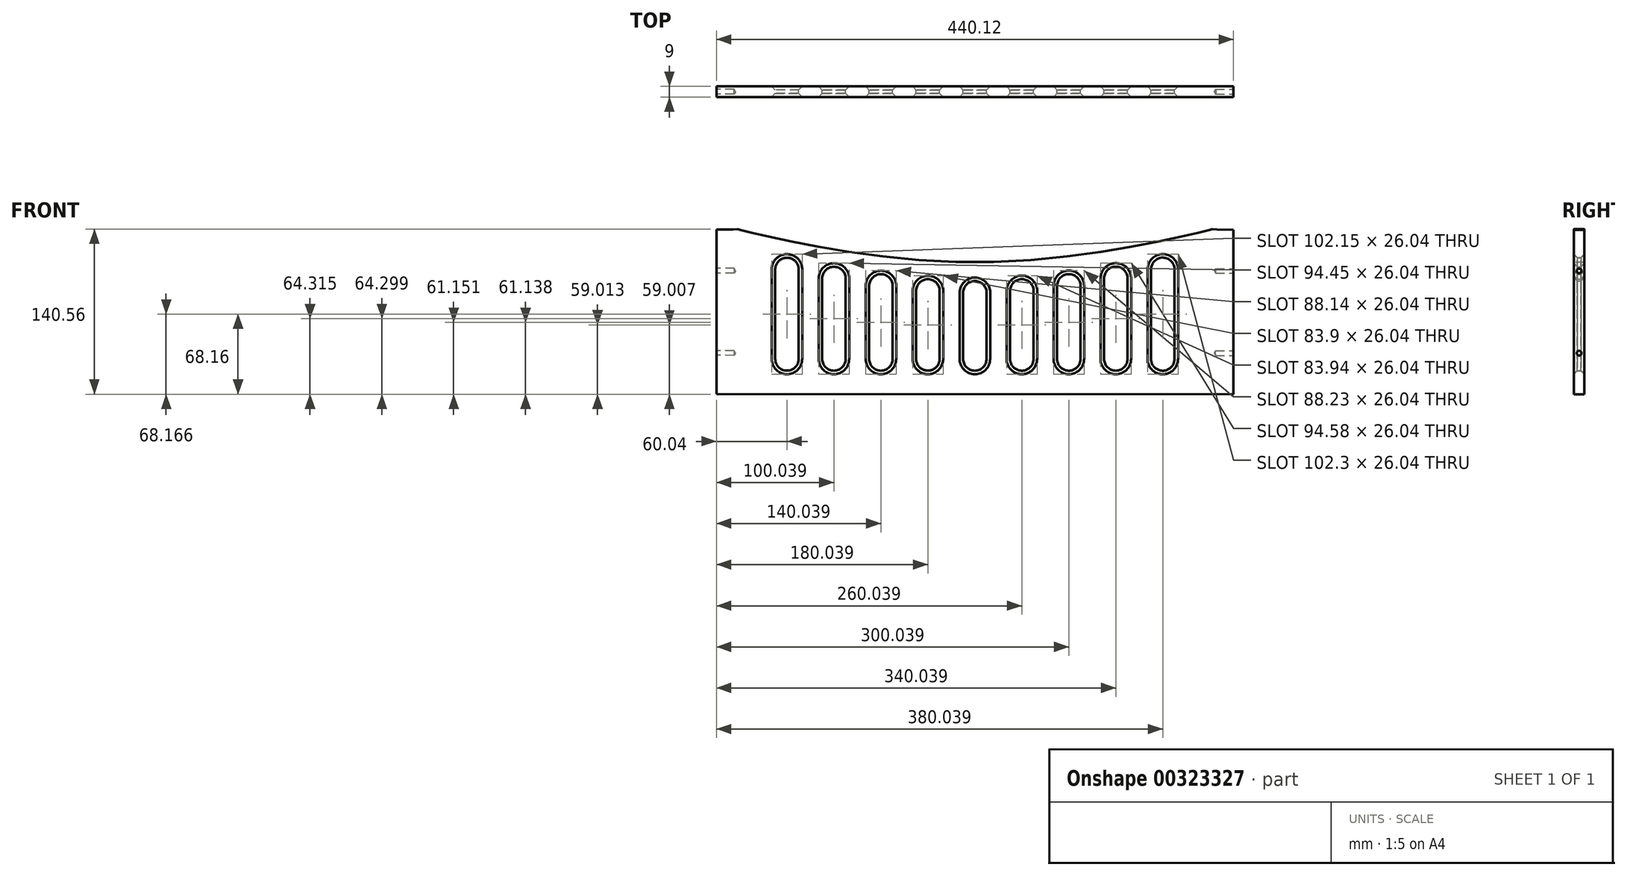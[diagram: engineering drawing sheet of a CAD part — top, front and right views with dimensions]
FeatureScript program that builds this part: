
annotation { "Feature Type Name" : "Feature", "Feature Type Description" : "" }
export const myFeature = defineFeature(function(context is Context, id is Id, definition is map)
    precondition{}
    {
        {
            var Q0;
            Q0=qCreatedBy(makeId("Front.planeOp"),FACE);
            var sketch = newSketch(context, id + "F0", { "sketchPlane" : qUnion([Q0])});
            skLineSegment(sketch, "E0.bottom", {"start": v(219.94, -70.05) * mm, "end": v(-220.06, -69.95) * mm});
            skLineSegment(sketch, "E0.left", {"start": v(219.94, -70.05) * mm, "end": v(220.06, 69.95) * mm});
            skLineSegment(sketch, "E0.right", {"start": v(-220.06, -69.95) * mm, "end": v(-219.94, 70.05) * mm});
            skPoint(sketch, "E0.middle", {"position": v(0, 0) * mm});
            skFitSpline(sketch, "E1", {"points": [v(-219.94, 70.05) * mm, v(-199.94, 70.05) * mm, v(0, 42.34) * mm, v(200.06, 70.05) * mm, v(220.06, 69.95) * mm], "startDerivative": vector(501.28, 0) * mm, "endDerivative": vector(501.28, -2.26) * mm});
            skLineSegment(sketch, "E2", {"start": v(0, 16.34) * mm, "end": v(-0.04, -40) * mm});
            skLineSegment(sketch, "E3.4.0.1", {"start": v(-170, 16.34) * mm, "end": v(-170, 16.34) * mm});
            skLineSegment(sketch, "E4", {"start": v(-120, 28.47) * mm, "end": v(-120.04, -39.98) * mm});
            skLineSegment(sketch, "E5", {"start": v(-80, 22.16) * mm, "end": v(-80.04, -39.98) * mm});
            skLineSegment(sketch, "E6", {"start": v(-40, 17.9) * mm, "end": v(-40.04, -40) * mm});
            skLineSegment(sketch, "E7", {"start": v(40, 17.93) * mm, "end": v(39.96, -40) * mm});
            skLineSegment(sketch, "E8", {"start": v(80, 22.22) * mm, "end": v(79.96, -40.02) * mm});
            skLineSegment(sketch, "E9", {"start": v(120, 28.55) * mm, "end": v(119.96, -40.02) * mm});
            skLineSegment(sketch, "E10", {"start": v(160, 36.27) * mm, "end": v(159.96, -40.03) * mm});
            skArc(sketch, "E11.0.startCap", {"start": v(-170, 36.19) * mm, "mid": v(-160, 46.18) * mm, "end": v(-150, 36.18) * mm});
            skArc(sketch, "E11.0.endCap", {"start": v(-150.05, -39.97) * mm, "mid": v(-160.05, -49.96) * mm, "end": v(-170.04, -39.96) * mm});
            skLineSegment(sketch, "E11.0.left", {"start": v(-150, 36.18) * mm, "end": v(-150.05, -39.97) * mm});
            skLineSegment(sketch, "E11.0.right", {"start": v(-170, 36.19) * mm, "end": v(-170.04, -39.96) * mm});
            skArc(sketch, "E11.1.startCap", {"start": v(-130, 28.48) * mm, "mid": v(-120, 38.47) * mm, "end": v(-110, 28.47) * mm});
            skArc(sketch, "E11.1.endCap", {"start": v(-110.04, -39.98) * mm, "mid": v(-120.05, -49.98) * mm, "end": v(-130.04, -39.97) * mm});
            skLineSegment(sketch, "E11.1.left", {"start": v(-110, 28.47) * mm, "end": v(-110.04, -39.98) * mm});
            skLineSegment(sketch, "E11.1.right", {"start": v(-130, 28.48) * mm, "end": v(-130.04, -39.97) * mm});
            skArc(sketch, "E11.2.startCap", {"start": v(-90, 22.17) * mm, "mid": v(-80, 32.16) * mm, "end": v(-70, 22.15) * mm});
            skArc(sketch, "E11.2.endCap", {"start": v(-70.04, -40) * mm, "mid": v(-80.05, -49.98) * mm, "end": v(-90.04, -39.98) * mm});
            skLineSegment(sketch, "E11.2.left", {"start": v(-70, 22.15) * mm, "end": v(-70.04, -40) * mm});
            skLineSegment(sketch, "E11.2.right", {"start": v(-90, 22.17) * mm, "end": v(-90.04, -39.98) * mm});
            skArc(sketch, "E11.3.startCap", {"start": v(-50, 17.91) * mm, "mid": v(-40, 27.9) * mm, "end": v(-30, 17.9) * mm});
            skArc(sketch, "E11.3.endCap", {"start": v(-30.04, -40) * mm, "mid": v(-40.05, -50) * mm, "end": v(-50.04, -39.98) * mm});
            skLineSegment(sketch, "E11.3.left", {"start": v(-30, 17.9) * mm, "end": v(-30.04, -40) * mm});
            skLineSegment(sketch, "E11.3.right", {"start": v(-50, 17.91) * mm, "end": v(-50.04, -39.98) * mm});
            skArc(sketch, "E11.4.startCap", {"start": v(-10, 16.34) * mm, "mid": v(0, 26.34) * mm, "end": v(10, 16.33) * mm});
            skArc(sketch, "E11.4.endCap", {"start": v(9.96, -40) * mm, "mid": v(-0.05, -50) * mm, "end": v(-10.04, -40) * mm});
            skLineSegment(sketch, "E11.4.left", {"start": v(10, 16.33) * mm, "end": v(9.96, -40) * mm});
            skLineSegment(sketch, "E11.4.right", {"start": v(-10, 16.34) * mm, "end": v(-10.04, -40) * mm});
            skArc(sketch, "E11.5.startCap", {"start": v(30, 17.94) * mm, "mid": v(40, 27.93) * mm, "end": v(50, 17.93) * mm});
            skArc(sketch, "E11.5.endCap", {"start": v(49.96, -40.02) * mm, "mid": v(39.95, -50) * mm, "end": v(29.96, -40) * mm});
            skLineSegment(sketch, "E11.5.left", {"start": v(50, 17.93) * mm, "end": v(49.96, -40.02) * mm});
            skLineSegment(sketch, "E11.5.right", {"start": v(30, 17.94) * mm, "end": v(29.96, -40) * mm});
            skArc(sketch, "E11.6.startCap", {"start": v(70, 22.23) * mm, "mid": v(80, 32.22) * mm, "end": v(90, 22.21) * mm});
            skArc(sketch, "E11.6.endCap", {"start": v(89.96, -40.02) * mm, "mid": v(79.95, -50.02) * mm, "end": v(69.96, -40) * mm});
            skLineSegment(sketch, "E11.6.left", {"start": v(90, 22.21) * mm, "end": v(89.96, -40.02) * mm});
            skLineSegment(sketch, "E11.6.right", {"start": v(70, 22.23) * mm, "end": v(69.96, -40) * mm});
            skArc(sketch, "E11.7.startCap", {"start": v(110, 28.56) * mm, "mid": v(120, 38.55) * mm, "end": v(130, 28.55) * mm});
            skArc(sketch, "E11.7.endCap", {"start": v(129.96, -40.03) * mm, "mid": v(119.95, -50.02) * mm, "end": v(109.96, -40.02) * mm});
            skLineSegment(sketch, "E11.7.left", {"start": v(130, 28.55) * mm, "end": v(129.96, -40.03) * mm});
            skLineSegment(sketch, "E11.7.right", {"start": v(110, 28.56) * mm, "end": v(109.96, -40.02) * mm});
            skArc(sketch, "E11.8.startCap", {"start": v(150, 36.27) * mm, "mid": v(160, 46.27) * mm, "end": v(170, 36.26) * mm});
            skArc(sketch, "E11.8.endCap", {"start": v(169.96, -40.04) * mm, "mid": v(159.95, -50.03) * mm, "end": v(149.96, -40.03) * mm});
            skLineSegment(sketch, "E11.8.left", {"start": v(170, 36.26) * mm, "end": v(169.96, -40.04) * mm});
            skLineSegment(sketch, "E11.8.right", {"start": v(150, 36.27) * mm, "end": v(149.96, -40.03) * mm});
            skSolve(sketch);
        }
        {
            var Q0;
            Q0=makeQuery(id+"F0.imprint","IMPRINT",FACE,{"disambiguationData":[TD([[makeQuery(id+"F0.imprint","IMPRINT",EDGE,{"derivedFrom":sQuery(id+"F0.wireOp",EDGE,"E0.bottom")}),-1.0]])]});
            extrude(context, id + "F1", {"entities" : qUnion([Q0]), "depth" : 9 * mm});
        }
        {
            var Q0;
            Q0=makeQuery(id+"F1.opExtrude","CAP_EDGE",EDGE,{"disambiguationData":[OSD([sQuery(id+"F0.wireOp",EDGE,"E11.0.startCap")])],"isStart":false});
            var Q1;
            Q1=makeQuery(id+"F1.opExtrude","CAP_EDGE",EDGE,{"disambiguationData":[OSD([sQuery(id+"F0.wireOp",EDGE,"E11.1.left")])],"isStart":false});
            var Q2;
            Q2=makeQuery(id+"F1.opExtrude","CAP_EDGE",EDGE,{"disambiguationData":[OSD([sQuery(id+"F0.wireOp",EDGE,"E11.2.left")])],"isStart":false});
            var Q3;
            Q3=makeQuery(id+"F1.opExtrude","CAP_EDGE",EDGE,{"disambiguationData":[OSD([sQuery(id+"F0.wireOp",EDGE,"E11.3.left")])],"isStart":false});
            var Q4;
            Q4=makeQuery(id+"F1.opExtrude","CAP_EDGE",EDGE,{"disambiguationData":[OSD([sQuery(id+"F0.wireOp",EDGE,"E11.4.left")])],"isStart":false});
            var Q5;
            Q5=makeQuery(id+"F1.opExtrude","CAP_EDGE",EDGE,{"disambiguationData":[OSD([sQuery(id+"F0.wireOp",EDGE,"E11.5.left")])],"isStart":true});
            var Q6;
            Q6=makeQuery(id+"F1.opExtrude","CAP_EDGE",EDGE,{"disambiguationData":[OSD([sQuery(id+"F0.wireOp",EDGE,"E11.5.left")])],"isStart":false});
            var Q7;
            Q7=makeQuery(id+"F1.opExtrude","CAP_EDGE",EDGE,{"disambiguationData":[OSD([sQuery(id+"F0.wireOp",EDGE,"E11.6.left")])],"isStart":true});
            var Q8;
            Q8=makeQuery(id+"F1.opExtrude","CAP_EDGE",EDGE,{"disambiguationData":[OSD([sQuery(id+"F0.wireOp",EDGE,"E11.6.left")])],"isStart":false});
            var Q9;
            Q9=makeQuery(id+"F1.opExtrude","CAP_EDGE",EDGE,{"disambiguationData":[OSD([sQuery(id+"F0.wireOp",EDGE,"E11.7.left")])],"isStart":false});
            var Q10;
            Q10=makeQuery(id+"F1.opExtrude","CAP_EDGE",EDGE,{"disambiguationData":[OSD([sQuery(id+"F0.wireOp",EDGE,"E11.7.left")])],"isStart":true});
            var Q11;
            Q11=makeQuery(id+"F1.opExtrude","CAP_EDGE",EDGE,{"disambiguationData":[OSD([sQuery(id+"F0.wireOp",EDGE,"E11.8.right")])],"isStart":false});
            var Q12;
            Q12=makeQuery(id+"F1.opExtrude","CAP_EDGE",EDGE,{"disambiguationData":[OSD([sQuery(id+"F0.wireOp",EDGE,"E11.8.left")])],"isStart":true});
            var Q13;
            Q13=makeQuery(id+"F1.opExtrude","CAP_EDGE",EDGE,{"disambiguationData":[OSD([sQuery(id+"F0.wireOp",EDGE,"E11.0.right")])],"isStart":true});
            var Q14;
            Q14=makeQuery(id+"F1.opExtrude","CAP_EDGE",EDGE,{"disambiguationData":[OSD([sQuery(id+"F0.wireOp",EDGE,"E11.1.right")])],"isStart":true});
            var Q15;
            Q15=makeQuery(id+"F1.opExtrude","CAP_EDGE",EDGE,{"disambiguationData":[OSD([sQuery(id+"F0.wireOp",EDGE,"E11.2.right")])],"isStart":true});
            var Q16;
            Q16=makeQuery(id+"F1.opExtrude","CAP_EDGE",EDGE,{"disambiguationData":[OSD([sQuery(id+"F0.wireOp",EDGE,"E11.3.right")])],"isStart":true});
            var Q17;
            Q17=makeQuery(id+"F1.opExtrude","CAP_EDGE",EDGE,{"disambiguationData":[OSD([sQuery(id+"F0.wireOp",EDGE,"E11.4.right")])],"isStart":true});
            chamfer(context, id + "F2", {"entities" : qUnion([Q0, Q1, Q2, Q3, Q4, Q5, Q6, Q7, Q8, Q9, Q10, Q11, Q12, Q13, Q14, Q15, Q16, Q17]), "width" : 3 * mm, "tangentPropagation" : true});
        }
        {
            var Q0;
            Q0=makeQuery(id+"F1.opExtrude","SWEPT_FACE",FACE,{"disambiguationData":[OSD([sQuery(id+"F0.wireOp",EDGE,"E0.right")])]});
            var sketch = newSketch(context, id + "F3", { "sketchPlane" : qUnion([Q0])});
            skLineSegment(sketch, "E12", {"start": v(4.5, 69.85) * mm, "end": v(4.5, -70.15) * mm});
            skPoint(sketch, "E13", {"position": v(4.5, 34.85) * mm});
            skPoint(sketch, "E14", {"position": v(4.5, -35.15) * mm});
            skSolve(sketch);
        }
        {
            var Q0;
            Q0=sQuery(id+"F3.wireOp",VERTEX,"E13");
            var Q1;
            Q1=sQuery(id+"F3.wireOp",VERTEX,"E14");
            var Q2;
            Q2=makeQuery(id+"F1.opExtrude","SWEPT_BODY",BODY,{"disambiguationData":[OSD([sQuery(id+"F0.wireOp",EDGE,"E0.bottom"),sQuery(id+"F0.wireOp",EDGE,"E0.left"),sQuery(id+"F0.wireOp",EDGE,"E0.right"),sQuery(id+"F0.wireOp",EDGE,"E1"),sQuery(id+"F0.wireOp",EDGE,"E11.0.startCap"),sQuery(id+"F0.wireOp",EDGE,"E11.0.endCap"),sQuery(id+"F0.wireOp",EDGE,"E11.0.left"),sQuery(id+"F0.wireOp",EDGE,"E11.0.right"),sQuery(id+"F0.wireOp",EDGE,"E11.1.startCap"),sQuery(id+"F0.wireOp",EDGE,"E11.1.endCap"),sQuery(id+"F0.wireOp",EDGE,"E11.1.left"),sQuery(id+"F0.wireOp",EDGE,"E11.1.right"),sQuery(id+"F0.wireOp",EDGE,"E11.2.startCap"),sQuery(id+"F0.wireOp",EDGE,"E11.2.endCap"),sQuery(id+"F0.wireOp",EDGE,"E11.2.left"),sQuery(id+"F0.wireOp",EDGE,"E11.2.right"),sQuery(id+"F0.wireOp",EDGE,"E11.3.startCap"),sQuery(id+"F0.wireOp",EDGE,"E11.3.endCap"),sQuery(id+"F0.wireOp",EDGE,"E11.3.left"),sQuery(id+"F0.wireOp",EDGE,"E11.3.right"),sQuery(id+"F0.wireOp",EDGE,"E11.4.startCap"),sQuery(id+"F0.wireOp",EDGE,"E11.4.endCap"),sQuery(id+"F0.wireOp",EDGE,"E11.4.left"),sQuery(id+"F0.wireOp",EDGE,"E11.4.right"),sQuery(id+"F0.wireOp",EDGE,"E11.5.startCap"),sQuery(id+"F0.wireOp",EDGE,"E11.5.endCap"),sQuery(id+"F0.wireOp",EDGE,"E11.5.left"),sQuery(id+"F0.wireOp",EDGE,"E11.5.right"),sQuery(id+"F0.wireOp",EDGE,"E11.6.startCap"),sQuery(id+"F0.wireOp",EDGE,"E11.6.endCap"),sQuery(id+"F0.wireOp",EDGE,"E11.6.left"),sQuery(id+"F0.wireOp",EDGE,"E11.6.right"),sQuery(id+"F0.wireOp",EDGE,"E11.7.startCap"),sQuery(id+"F0.wireOp",EDGE,"E11.7.endCap"),sQuery(id+"F0.wireOp",EDGE,"E11.7.left"),sQuery(id+"F0.wireOp",EDGE,"E11.7.right"),sQuery(id+"F0.wireOp",EDGE,"E11.8.startCap"),sQuery(id+"F0.wireOp",EDGE,"E11.8.endCap"),sQuery(id+"F0.wireOp",EDGE,"E11.8.left"),sQuery(id+"F0.wireOp",EDGE,"E11.8.right")])]});
            hole(context, id + "F4", {"style" : HoleStyle.SIMPLE, "endStyle" : HoleEndStyle.BLIND, "holeDiameter" : 4 * mm, "holeDepth" : 15 * mm, "tappedDepth" : 12 * mm, "tapClearance" : 3, "locations" : qUnion([Q0, Q1]), "scope" : qUnion([Q2])});
        }
        {
            var Q0;
            Q0=makeQuery(id+"F1.opExtrude","SWEPT_FACE",FACE,{"disambiguationData":[OSD([sQuery(id+"F0.wireOp",EDGE,"E0.left")])]});
            var sketch = newSketch(context, id + "F5", { "sketchPlane" : qUnion([Q0])});
            skLineSegment(sketch, "E15", {"start": v(-4.5, 70.15) * mm, "end": v(-4.5, -69.85) * mm});
            skPoint(sketch, "E16", {"position": v(-4.5, 35.15) * mm});
            skPoint(sketch, "E17", {"position": v(-4.5, -34.85) * mm});
            skSolve(sketch);
        }
        {
            var Q0;
            Q0=sQuery(id+"F5.wireOp",VERTEX,"E16");
            var Q1;
            Q1=sQuery(id+"F5.wireOp",VERTEX,"E17");
            var Q2;
            Q2=makeQuery(id+"F1.opExtrude","SWEPT_BODY",BODY,{"disambiguationData":[OSD([sQuery(id+"F0.wireOp",EDGE,"E0.bottom"),sQuery(id+"F0.wireOp",EDGE,"E0.left"),sQuery(id+"F0.wireOp",EDGE,"E0.right"),sQuery(id+"F0.wireOp",EDGE,"E1"),sQuery(id+"F0.wireOp",EDGE,"E11.0.startCap"),sQuery(id+"F0.wireOp",EDGE,"E11.0.endCap"),sQuery(id+"F0.wireOp",EDGE,"E11.0.left"),sQuery(id+"F0.wireOp",EDGE,"E11.0.right"),sQuery(id+"F0.wireOp",EDGE,"E11.1.startCap"),sQuery(id+"F0.wireOp",EDGE,"E11.1.endCap"),sQuery(id+"F0.wireOp",EDGE,"E11.1.left"),sQuery(id+"F0.wireOp",EDGE,"E11.1.right"),sQuery(id+"F0.wireOp",EDGE,"E11.2.startCap"),sQuery(id+"F0.wireOp",EDGE,"E11.2.endCap"),sQuery(id+"F0.wireOp",EDGE,"E11.2.left"),sQuery(id+"F0.wireOp",EDGE,"E11.2.right"),sQuery(id+"F0.wireOp",EDGE,"E11.3.startCap"),sQuery(id+"F0.wireOp",EDGE,"E11.3.endCap"),sQuery(id+"F0.wireOp",EDGE,"E11.3.left"),sQuery(id+"F0.wireOp",EDGE,"E11.3.right"),sQuery(id+"F0.wireOp",EDGE,"E11.4.startCap"),sQuery(id+"F0.wireOp",EDGE,"E11.4.endCap"),sQuery(id+"F0.wireOp",EDGE,"E11.4.left"),sQuery(id+"F0.wireOp",EDGE,"E11.4.right"),sQuery(id+"F0.wireOp",EDGE,"E11.5.startCap"),sQuery(id+"F0.wireOp",EDGE,"E11.5.endCap"),sQuery(id+"F0.wireOp",EDGE,"E11.5.left"),sQuery(id+"F0.wireOp",EDGE,"E11.5.right"),sQuery(id+"F0.wireOp",EDGE,"E11.6.startCap"),sQuery(id+"F0.wireOp",EDGE,"E11.6.endCap"),sQuery(id+"F0.wireOp",EDGE,"E11.6.left"),sQuery(id+"F0.wireOp",EDGE,"E11.6.right"),sQuery(id+"F0.wireOp",EDGE,"E11.7.startCap"),sQuery(id+"F0.wireOp",EDGE,"E11.7.endCap"),sQuery(id+"F0.wireOp",EDGE,"E11.7.left"),sQuery(id+"F0.wireOp",EDGE,"E11.7.right"),sQuery(id+"F0.wireOp",EDGE,"E11.8.startCap"),sQuery(id+"F0.wireOp",EDGE,"E11.8.endCap"),sQuery(id+"F0.wireOp",EDGE,"E11.8.left"),sQuery(id+"F0.wireOp",EDGE,"E11.8.right")])]});
            hole(context, id + "F6", {"style" : HoleStyle.SIMPLE, "endStyle" : HoleEndStyle.BLIND, "holeDiameter" : 4 * mm, "holeDepth" : 15 * mm, "tappedDepth" : 12 * mm, "tapClearance" : 3, "locations" : qUnion([Q0, Q1]), "scope" : qUnion([Q2])});
        }
    });
